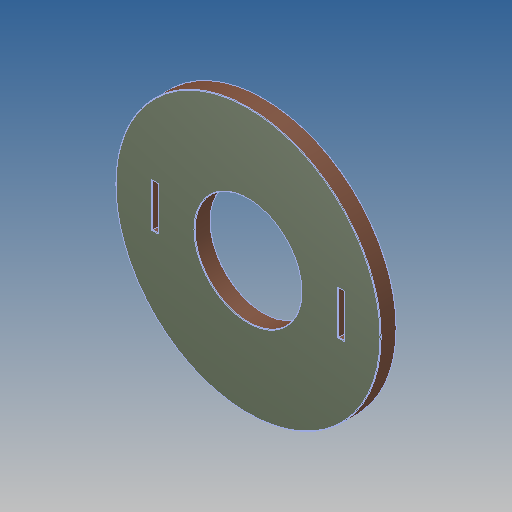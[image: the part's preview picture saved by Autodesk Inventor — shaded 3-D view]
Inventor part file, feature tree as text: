
AUTODESK INVENTOR PART (.ipt)
format: ipt  version: 2020 (Build 240168000, 168)  size: 143,872 bytes
history: mixed  units: mm
features: other x1, fillet x1, imported_body x1
ambient origin geometry x8: Origin, YZ Plane, XZ Plane, XY Plane, X Axis, Y Axis, Z Axis, Center Point
bodies: Body1 (imported_parasolid)
feature tree (3):
  other  "Твердое тело1"
  fillet  "Fillet1"  [1 undecoded]
  imported_body  NMx_Import_Brep_tag  [imported B-rep: ~32 faces, bbox_mm=[21.4, 4.1, 1.5]]
note: 1 required parameter value undecoded (feature->parameter linkage not recoverable at this tier; creation-order binding heuristic only, values carry confidence <= 0.55)
